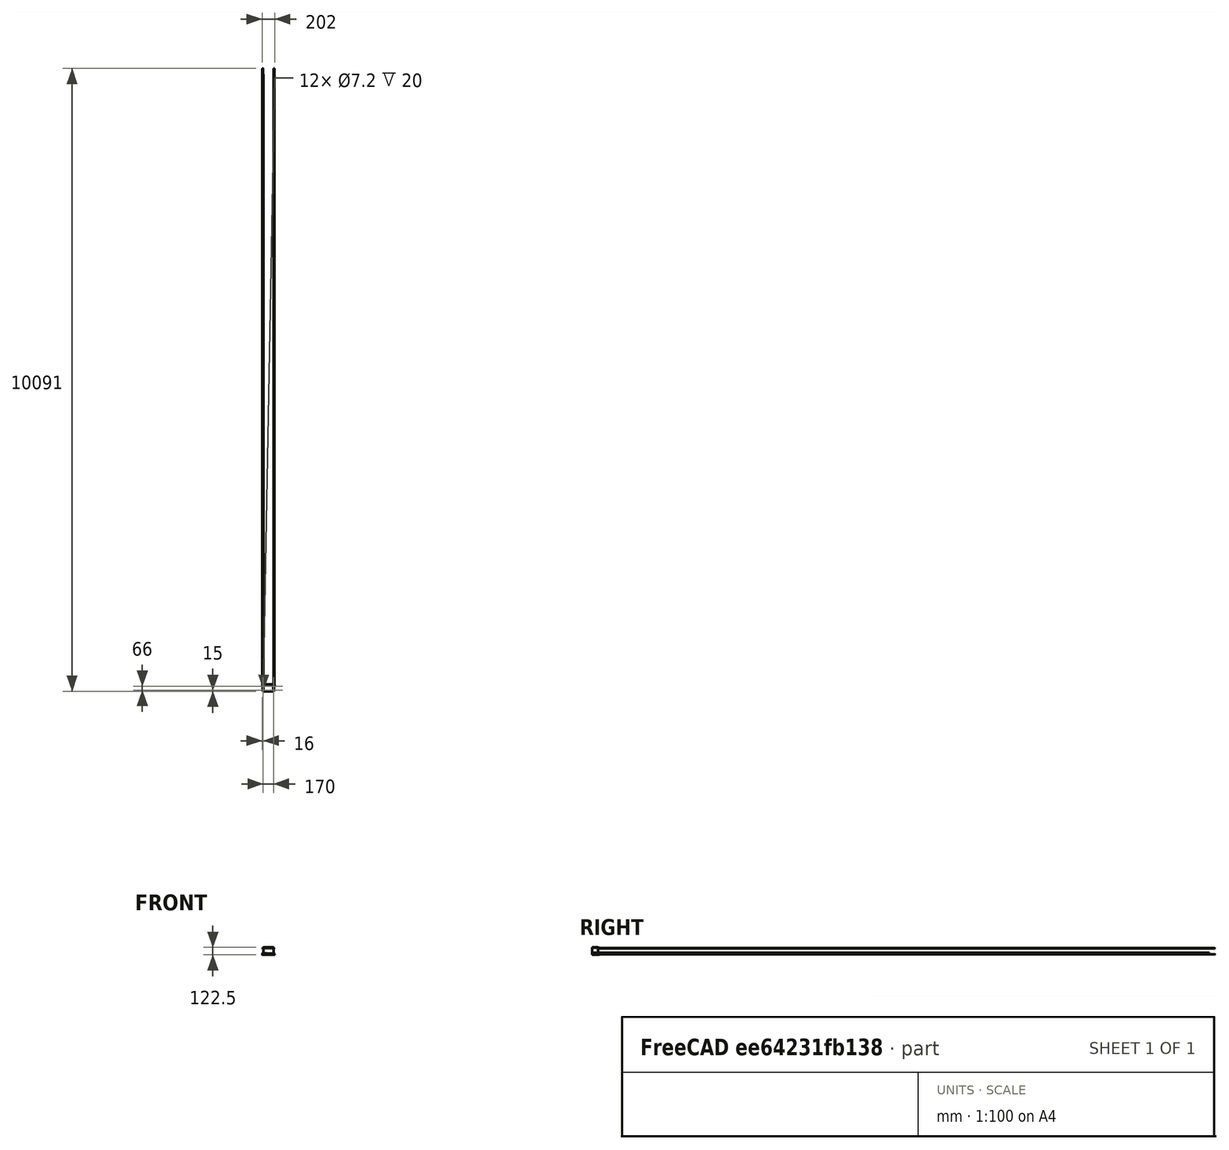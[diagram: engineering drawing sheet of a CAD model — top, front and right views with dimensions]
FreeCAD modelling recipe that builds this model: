
FCSTD DOCUMENT  (FreeCAD 0.15R4671 (Git))
Label: EBOX_Bottom
License: All rights reserved
LicenseURL: http://en.wikipedia.org/wiki/All_rights_reserved
objects: Sketcher::SketchObject×14, PartDesign::Pocket×9, PartDesign::Fillet×6, Mesh::Feature×5, PartDesign::Pad×5, Part::Feature×4
note: 52 computed .brp shape members not serialized (recipe doc carries the construction recipe); baked Part::Feature solids carry a one-line shape summary decoded from their .brp

FEATURE [Part::Feature] Part__Feature003  label="MKS_Gen_V1p3"
  Placement = pos=(4,-58,9) rot=(0,0,1;0rad)
  shape: bbox 143.1 x 84.2 x 22.31 mm, 8746 faces, 0 solids (baked)
FEATURE [Part::Feature] Part__Feature  label="OB1515_180mm"
  Placement = pos=(-90,0,0) rot=(0,1,0;1.5708rad)
  shape: bbox 180 x 15 x 15 mm, 158 faces (baked)
FEATURE [Part::Feature] Part__Feature004  label="OB1515_180mm001"
  Placement = pos=(-90,0,100) rot=(0,1,0;1.5708rad)
  shape: bbox 180 x 15 x 15 mm, 158 faces (baked)
FEATURE [Mesh::Feature] _0mmFan  label="40mmFan"
  Placement = pos=(15,-41,56) rot=(0,0,1;0rad)
FEATURE [Sketcher::SketchObject] Sketch
  Placement = pos=(0,0,-7.5) rot=(0,0,1;0rad)
  sketch-geometry (4):
    g0: LineSegment StartX=82 StartY=-8 StartZ=0 EndX=-82 EndY=-8 EndZ=0
    g1: LineSegment StartX=-82 StartY=-8 StartZ=0 EndX=-82 EndY=-106 EndZ=0
    g2: LineSegment StartX=-82 StartY=-106 StartZ=0 EndX=82 EndY=-106 EndZ=0
    g3: LineSegment StartX=82 StartY=-106 StartZ=0 EndX=82 EndY=-8 EndZ=0
  constraints (8):
    c: Coincident(g0,g1)
    c: Coincident(g1,g2)
    c: Coincident(g2,g3)
    c: Coincident(g3,g0)
    c: Horizontal(g0)
    c: Horizontal(g2)
    c: Vertical(g1)
    c: Vertical(g3)
FEATURE [PartDesign::Pad] Pad
  Length = 115
  Length2 = 100
  Placement = pos=(0,0,-7.5) rot=(0,0,1;0rad)
  Sketch = -> Sketch
  Type = 0
FEATURE [Sketcher::SketchObject] Sketch001
  Placement = pos=(0,0,107.5) rot=(0,0,1;0rad)
  Support = -> Pad [Face6]
  sketch-geometry (4):
    g0: LineSegment StartX=-79 StartY=-11 StartZ=0 EndX=79 EndY=-11 EndZ=0
    g1: LineSegment StartX=79 StartY=-11 StartZ=0 EndX=79 EndY=-103 EndZ=0
    g2: LineSegment StartX=79 StartY=-103 StartZ=0 EndX=-79 EndY=-103 EndZ=0
    g3: LineSegment StartX=-79 StartY=-103 StartZ=0 EndX=-79 EndY=-11 EndZ=0
  constraints (8):
    c: Coincident(g0,g1)
    c: Coincident(g1,g2)
    c: Coincident(g2,g3)
    c: Coincident(g3,g0)
    c: Horizontal(g0)
    c: Horizontal(g2)
    c: Vertical(g1)
    c: Vertical(g3)
FEATURE [PartDesign::Pocket] Pocket
  Length = 112
  Placement = pos=(0,0,-7.5) rot=(0,0,1;0rad)
  Sketch = -> Sketch001
  Type = 0
FEATURE [Sketcher::SketchObject] Sketch002
  Placement = pos=(0,0,-4.5) rot=(0,0,1;0rad)
  Support = -> Pocket [Face11]
  sketch-geometry (4):
    g0: Circle CenterX=71.2811 CenterY=-20.1362 CenterZ=0 NormalX=0 NormalY=0 NormalZ=1 Radius=4
    g1: Circle CenterX=71.2541 CenterY=-95.8403 CenterZ=0 NormalX=0 NormalY=0 NormalZ=1 Radius=4
    g2: Circle CenterX=-63.2692 CenterY=-95.845 CenterZ=0 NormalX=0 NormalY=0 NormalZ=1 Radius=4
    g3: Circle CenterX=-63.279 CenterY=-20.1649 CenterZ=0 NormalX=0 NormalY=0 NormalZ=1 Radius=4
  constraints (4):
    c: Radius(g0) = 4
    c: Equal(g0,g1)
    c: Equal(g0,g2)
    c: Equal(g0,g3)
FEATURE [PartDesign::Pad] Pad001
  Length = 13.5
  Length2 = 100
  Placement = pos=(0,0,-7.5) rot=(0,0,1;0rad)
  Sketch = -> Sketch002
  Type = 0
FEATURE [Sketcher::SketchObject] Sketch003
  Placement = pos=(0,0,9) rot=(0,0,1;0rad)
  Support = -> Pad001 [Face17]
  sketch-geometry (4):
    g0: Circle CenterX=-63.2989 CenterY=-20.1665 CenterZ=0 NormalX=0 NormalY=0 NormalZ=1 Radius=1.5
    g1: Circle CenterX=71.3054 CenterY=-20.1275 CenterZ=0 NormalX=0 NormalY=0 NormalZ=1 Radius=1.5
    g2: Circle CenterX=71.282 CenterY=-95.8363 CenterZ=0 NormalX=0 NormalY=0 NormalZ=1 Radius=1.5
    g3: Circle CenterX=-63.2831 CenterY=-95.8609 CenterZ=0 NormalX=0 NormalY=0 NormalZ=1 Radius=1.5
  constraints (4):
    c: Radius(g0) = 1.5
    c: Equal(g0,g1)
    c: Equal(g0,g2)
    c: Equal(g0,g3)
FEATURE [PartDesign::Pocket] Pocket001
  Length = 8
  Placement = pos=(0,0,-7.5) rot=(0,0,1;0rad)
  Sketch = -> Sketch003
  Type = 0
FEATURE [Sketcher::SketchObject] Sketch004
  Placement = pos=(0,0,107.5) rot=(0,0,1;0rad)
  Support = -> Pocket001 [Face5]
  sketch-geometry (4):
    g0: LineSegment StartX=-82 StartY=-106 StartZ=0 EndX=82 EndY=-106 EndZ=0
    g1: LineSegment StartX=82 StartY=-106 StartZ=0 EndX=82 EndY=-8 EndZ=0
    g2: LineSegment StartX=82 StartY=-8 StartZ=0 EndX=-82 EndY=-8 EndZ=0
    g3: LineSegment StartX=-82 StartY=-8 StartZ=0 EndX=-82 EndY=-106 EndZ=0
  constraints (8):
    c: Coincident(g0,g1)
    c: Coincident(g1,g2)
    c: Coincident(g2,g3)
    c: Coincident(g3,g0)
    c: Horizontal(g0)
    c: Horizontal(g2)
    c: Vertical(g1)
    c: Vertical(g3)
FEATURE [PartDesign::Pad] Pad002
  Length = 3
  Length2 = 100
  Placement = pos=(0,0,-7.5) rot=(0,0,1;0rad)
  Reversed = true
  Sketch = -> Sketch004
  Type = 0
FEATURE [Part::Feature] Pad002001  label="Pad003"
  shape: bbox 164 x 98 x 115 mm, 28 faces (baked)
FEATURE [Sketcher::SketchObject] Sketch005
  Placement = pos=(0,0,-7.5) rot=(1,0,0;3.14159rad)
  Support = -> Pad002001 [Face1]
  sketch-geometry (16):
    g0: ArcOfCircle CenterX=84 CenterY=25 CenterZ=0 NormalX=0 NormalY=0 NormalZ=1 Radius=7 StartAngle=4.71239 EndAngle=7.85398
    g1: ArcOfCircle CenterX=84 CenterY=91 CenterZ=0 NormalX=0 NormalY=0 NormalZ=1 Radius=7 StartAngle=4.71239 EndAngle=7.85398
    g2: ArcOfCircle CenterX=-84 CenterY=91 CenterZ=0 NormalX=0 NormalY=0 NormalZ=1 Radius=7 StartAngle=1.5708 EndAngle=4.71239
    g3: ArcOfCircle CenterX=-84 CenterY=25 CenterZ=0 NormalX=0 NormalY=0 NormalZ=1 Radius=7 StartAngle=1.5708 EndAngle=4.71239
    g4: LineSegment StartX=-84 StartY=32 StartZ=0 EndX=-81 EndY=32 EndZ=0
    g5: LineSegment StartX=-81 StartY=32 StartZ=0 EndX=-81 EndY=18 EndZ=0
    g6: LineSegment StartX=-81 StartY=18 StartZ=0 EndX=-84 EndY=18 EndZ=0
    g7: LineSegment StartX=-84 StartY=98 StartZ=0 EndX=-81 EndY=98 EndZ=0
    g8: LineSegment StartX=-81 StartY=98 StartZ=0 EndX=-81 EndY=84 EndZ=0
    g9: LineSegment StartX=-81 StartY=84 StartZ=0 EndX=-84 EndY=84 EndZ=0
    g10: LineSegment StartX=84 StartY=98 StartZ=0 EndX=81 EndY=98 EndZ=0
    g11: LineSegment StartX=81 StartY=98 StartZ=0 EndX=81 EndY=84 EndZ=0
    g12: LineSegment StartX=81 StartY=84 StartZ=0 EndX=84 EndY=84 EndZ=0
    g13: LineSegment StartX=84 StartY=32 StartZ=0 EndX=81 EndY=32 EndZ=0
    g14: LineSegment StartX=81 StartY=32 StartZ=0 EndX=81 EndY=18 EndZ=0
    g15: LineSegment StartX=81 StartY=18 StartZ=0 EndX=84 EndY=18 EndZ=0
  constraints (25):
    c: Tangent(g3,g4) = 1.5708
    c: Coincident(g4,g5)
    c: Vertical(g5)
    c: Coincident(g5,g6)
    c: Coincident(g6,g3)
    c: Horizontal(g6)
    c: Tangent(g6,g3)
    c: Tangent(g2,g7) = 1.5708
    c: Coincident(g7,g8)
    c: Vertical(g8)
    c: Coincident(g8,g9)
    c: Coincident(g9,g2)
    c: Horizontal(g9)
    c: Tangent(g1,g10) = -1.5708
    c: Coincident(g10,g11)
    c: Vertical(g11)
    c: Coincident(g11,g12)
    c: Coincident(g12,g1)
    c: Horizontal(g12)
    c: Tangent(g0,g13) = -1.5708
    c: Coincident(g13,g14)
    c: Vertical(g14)
    c: Coincident(g14,g15)
    c: Coincident(g15,g0)
    c: Horizontal(g15)
FEATURE [PartDesign::Pad] Pad002002
  Length = 35
  Length2 = 100
  Reversed = true
  Sketch = -> Sketch005
  Type = 0
FEATURE [PartDesign::Fillet] Fillet
  Base = -> Pad002002 [Edge28,Edge26,Edge22,Edge24,Edge8,Edge12,Edge14,Edge10]
  Radius = 1.99
FEATURE [Sketcher::SketchObject] Sketch006
  Placement = pos=(0,-106,0) rot=(1,0,0;1.5708rad)
  Support = -> Fillet [Face7]
  sketch-geometry (10):
    g0: LineSegment StartX=-82 StartY=29 StartZ=0 EndX=-82 EndY=27 EndZ=0
    g1: LineSegment StartX=-82 StartY=27 StartZ=0 EndX=-91 EndY=18 EndZ=0
    g2: LineSegment StartX=-91 StartY=18 StartZ=0 EndX=-92 EndY=18 EndZ=0
    g3: LineSegment StartX=-92 StartY=18 StartZ=0 EndX=-92 EndY=29 EndZ=0
    g4: LineSegment StartX=-92 StartY=29 StartZ=0 EndX=-82 EndY=29 EndZ=0
    g5: LineSegment StartX=82 StartY=29 StartZ=0 EndX=82 EndY=27 EndZ=0
    g6: LineSegment StartX=82 StartY=27 StartZ=0 EndX=91 EndY=18 EndZ=0
    g7: LineSegment StartX=91 StartY=18 StartZ=0 EndX=92 EndY=18 EndZ=0
    g8: LineSegment StartX=92 StartY=18 StartZ=0 EndX=92 EndY=29 EndZ=0
    g9: LineSegment StartX=92 StartY=29 StartZ=0 EndX=82 EndY=29 EndZ=0
  constraints (18):
    c: Vertical(g0)
    c: Coincident(g0,g1)
    c: Coincident(g1,g2)
    c: Horizontal(g2)
    c: Coincident(g2,g3)
    c: Vertical(g3)
    c: Coincident(g3,g4)
    c: Coincident(g4,g0)
    c: Horizontal(g4)
    c: Vertical(g5)
    c: Coincident(g5,g6)
    c: Coincident(g6,g7)
    c: Horizontal(g7)
    c: Coincident(g7,g8)
    c: Vertical(g8)
    c: Coincident(g8,g9)
    c: Coincident(g9,g5)
    c: Horizontal(g9)
FEATURE [PartDesign::Pocket] Pocket002
  Length = 5
  Sketch = -> Sketch006
  Type = 1
FEATURE [Mesh::Feature] HexNutStyle1_M3
  Placement = pos=(86.28,1.15,-100) rot=(0,0,1;0.523599rad)
FEATURE [Mesh::Feature] HexNutStyle1_M
  Placement = pos=(86.28,-64.85,-100) rot=(0,0,1;0.523599rad)
FEATURE [Mesh::Feature] HexNutStyle1_M004
  Placement = pos=(-83.72,1.15,-100) rot=(0,0,1;0.523599rad)
FEATURE [Mesh::Feature] HexNutStyle1_M005
  Placement = pos=(-83.72,-64.85,-100) rot=(0,0,1;0.523599rad)
FEATURE [Sketcher::SketchObject] Sketch007
  Placement = pos=(0,0,-7.5) rot=(1,0,0;3.14159rad)
  Support = -> Pocket002 [Face2]
  sketch-geometry (4):
    g0: Circle CenterX=-85 CenterY=91 CenterZ=0 NormalX=0 NormalY=0 NormalZ=1 Radius=1.8
    g1: Circle CenterX=-85 CenterY=25 CenterZ=0 NormalX=0 NormalY=0 NormalZ=1 Radius=1.8
    g2: Circle CenterX=85 CenterY=25 CenterZ=0 NormalX=0 NormalY=0 NormalZ=1 Radius=1.8
    g3: Circle CenterX=85 CenterY=91 CenterZ=0 NormalX=0 NormalY=0 NormalZ=1 Radius=1.8
  constraints (4):
    c: Radius(g0) = 1.8
    c: Equal(g0,g1)
    c: Equal(g0,g2)
    c: Equal(g0,g3)
FEATURE [PartDesign::Pocket] Pocket003
  Length = 28
  Sketch = -> Sketch007
  Type = 0
FEATURE [Sketcher::SketchObject] Sketch008
  Placement = pos=(0,0,-7.5) rot=(1,0,0;3.14159rad)
  Support = -> Pocket003 [Face2]
  sketch-geometry (4):
    g0: Circle CenterX=85 CenterY=91 CenterZ=0 NormalX=0 NormalY=0 NormalZ=1 Radius=3.6
    g1: Circle CenterX=85 CenterY=25 CenterZ=0 NormalX=0 NormalY=0 NormalZ=1 Radius=3.6
    g2: Circle CenterX=-85 CenterY=91 CenterZ=0 NormalX=0 NormalY=0 NormalZ=1 Radius=3.6
    g3: Circle CenterX=-85 CenterY=25 CenterZ=0 NormalX=0 NormalY=0 NormalZ=1 Radius=3.6
  constraints (4):
    c: Radius(g0) = 3.6
    c: Equal(g0,g1)
    c: Equal(g0,g2)
    c: Equal(g0,g3)
FEATURE [PartDesign::Pocket] Pocket004
  Length = 20
  Sketch = -> Sketch008
  Type = 0
FEATURE [Sketcher::SketchObject] Sketch009
  Placement = pos=(0,-8,0) rot=(0,0.707107,0.707107;3.14159rad)
  Support = -> Pocket004 [Face1]
  sketch-geometry (16):
    g0: LineSegment StartX=-81 StartY=7.5 StartZ=0 EndX=-101 EndY=7.5 EndZ=0
    g1: LineSegment StartX=-101 StartY=7.5 StartZ=0 EndX=-101 EndY=-7.5 EndZ=0
    g2: LineSegment StartX=-101 StartY=-7.5 StartZ=0 EndX=-81 EndY=-7.5 EndZ=0
    g3: LineSegment StartX=-81 StartY=-7.5 StartZ=0 EndX=-81 EndY=7.5 EndZ=0
    g4: LineSegment StartX=81 StartY=7.5 StartZ=0 EndX=101 EndY=7.5 EndZ=0
    g5: LineSegment StartX=101 StartY=7.5 StartZ=0 EndX=101 EndY=-7.5 EndZ=0
    g6: LineSegment StartX=101 StartY=-7.5 StartZ=0 EndX=81 EndY=-7.5 EndZ=0
    g7: LineSegment StartX=81 StartY=-7.5 StartZ=0 EndX=81 EndY=7.5 EndZ=0
    g8: LineSegment StartX=-92 StartY=107.5 StartZ=0 EndX=-81 EndY=107.5 EndZ=0
    g9: LineSegment StartX=-81 StartY=107.5 StartZ=0 EndX=-81 EndY=92.5 EndZ=0
    g10: LineSegment StartX=-81 StartY=92.5 StartZ=0 EndX=-92 EndY=92.5 EndZ=0
    g11: LineSegment StartX=-92 StartY=92.5 StartZ=0 EndX=-92 EndY=107.5 EndZ=0
    g12: LineSegment StartX=81 StartY=92.5 StartZ=0 EndX=92 EndY=92.5 EndZ=0
    g13: LineSegment StartX=92 StartY=92.5 StartZ=0 EndX=92 EndY=107.5 EndZ=0
    g14: LineSegment StartX=92 StartY=107.5 StartZ=0 EndX=81 EndY=107.5 EndZ=0
    g15: LineSegment StartX=81 StartY=107.5 StartZ=0 EndX=81 EndY=92.5 EndZ=0
  constraints (32):
    c: Coincident(g0,g1)
    c: Coincident(g1,g2)
    c: Coincident(g2,g3)
    c: Coincident(g3,g0)
    c: Horizontal(g0)
    c: Horizontal(g2)
    c: Vertical(g1)
    c: Vertical(g3)
    c: Coincident(g4,g5)
    c: Coincident(g5,g6)
    c: Coincident(g6,g7)
    c: Coincident(g7,g4)
    c: Horizontal(g4)
    c: Horizontal(g6)
    c: Vertical(g5)
    c: Vertical(g7)
    c: Coincident(g8,g9)
    c: Coincident(g9,g10)
    c: Coincident(g10,g11)
    c: Coincident(g11,g8)
    c: Horizontal(g8)
    c: Horizontal(g10)
    c: Vertical(g9)
    c: Vertical(g11)
    c: Coincident(g12,g13)
    c: Coincident(g13,g14)
    c: Coincident(g14,g15)
    c: Coincident(g15,g12)
    c: Horizontal(g12)
    c: Horizontal(g14)
    c: Vertical(g13)
    c: Vertical(g15)
FEATURE [PartDesign::Pad] Pad002003
  Length = 7
  Length2 = 100
  Reversed = true
  Sketch = -> Sketch009
  Type = 0
FEATURE [PartDesign::Fillet] Fillet001
  Base = -> Pad002003 [Edge22,Edge63]
  Radius = 4
FEATURE [PartDesign::Fillet] Fillet002
  Base = -> Fillet001 [Edge111,Edge77,Edge88,Edge51,Edge112,Edge78,Edge128,Edge92]
  Radius = 4
FEATURE [PartDesign::Fillet] Fillet003
  Base = -> Fillet002 [Edge120,Edge46]
  Radius = 4
FEATURE [Sketcher::SketchObject] Sketch010
  Placement = pos=(0,-15,0) rot=(1,0,0;1.5708rad)
  Support = -> Fillet003 [Face35]
  sketch-geometry (4):
    g0: Circle CenterX=-87.5 CenterY=100 CenterZ=0 NormalX=0 NormalY=0 NormalZ=1 Radius=1.8
    g1: Circle CenterX=87.5 CenterY=100 CenterZ=0 NormalX=0 NormalY=0 NormalZ=1 Radius=1.8
    g2: Circle CenterX=95 CenterY=0 CenterZ=0 NormalX=0 NormalY=0 NormalZ=1 Radius=1.8
    g3: Circle CenterX=-95 CenterY=0 CenterZ=0 NormalX=0 NormalY=0 NormalZ=1 Radius=1.8
  constraints (6):
    c: PointOnObject(g2,g-1)
    c: PointOnObject(g3,g-1)
    c: Radius(g0) = 1.8
    c: Equal(g0,g1)
    c: Equal(g0,g2)
    c: Equal(g0,g3)
FEATURE [PartDesign::Pocket] Pocket005
  Length = 5
  Sketch = -> Sketch010
  Type = 1
FEATURE [Sketcher::SketchObject] Sketch011
  Placement = pos=(0,-15,0) rot=(1,0,0;1.5708rad)
  Support = -> Pocket005 [Face31]
  sketch-geometry (4):
    g0: Circle CenterX=-87.5 CenterY=100 CenterZ=0 NormalX=0 NormalY=0 NormalZ=1 Radius=3.5
    g1: Circle CenterX=87.5 CenterY=100 CenterZ=0 NormalX=0 NormalY=0 NormalZ=1 Radius=3.5
    g2: Circle CenterX=95 CenterY=0 CenterZ=0 NormalX=0 NormalY=0 NormalZ=1 Radius=3.5
    g3: Circle CenterX=-95 CenterY=0 CenterZ=0 NormalX=0 NormalY=0 NormalZ=1 Radius=3.5
  constraints (6):
    c: PointOnObject(g2,g-1)
    c: PointOnObject(g3,g-1)
    c: Radius(g0) = 3.5
    c: Equal(g0,g1)
    c: Equal(g0,g2)
    c: Equal(g0,g3)
FEATURE [PartDesign::Pocket] Pocket006
  Length = 3
  Sketch = -> Sketch011
  Type = 0
FEATURE [PartDesign::Fillet] Fillet004
  Base = -> Pocket006 [Edge49,Edge45,Edge78,Edge79,Edge139]
  Radius = 1
FEATURE [Sketcher::SketchObject] Sketch012
  Placement = pos=(0,-106,0) rot=(1,0,0;1.5708rad)
  Support = -> Fillet004 [Face26]
  sketch-geometry (4):
    g0: LineSegment StartX=-46 StartY=21.5 StartZ=0 EndX=-33.5 EndY=21.5 EndZ=0
    g1: LineSegment StartX=-33.5 StartY=21.5 StartZ=0 EndX=-33.5 EndY=10.5 EndZ=0
    g2: LineSegment StartX=-33.5 StartY=10.5 StartZ=0 EndX=-46 EndY=10.5 EndZ=0
    g3: LineSegment StartX=-46 StartY=10.5 StartZ=0 EndX=-46 EndY=21.5 EndZ=0
  constraints (8):
    c: Coincident(g0,g1)
    c: Coincident(g1,g2)
    c: Coincident(g2,g3)
    c: Coincident(g3,g0)
    c: Horizontal(g0)
    c: Horizontal(g2)
    c: Vertical(g1)
    c: Vertical(g3)
FEATURE [PartDesign::Pocket] Pocket007
  Length = 5
  Sketch = -> Sketch012
  Type = 0
FEATURE [Sketcher::SketchObject] Sketch013
  Placement = pos=(0,-106,0) rot=(1,0,0;1.5708rad)
  Support = -> Pocket007 [Face22]
  sketch-geometry (4):
    g0: LineSegment StartX=-111 StartY=123 StartZ=0 EndX=97 EndY=123 EndZ=0
    g1: LineSegment StartX=97 StartY=123 StartZ=0 EndX=97 EndY=14.5 EndZ=0
    g2: LineSegment StartX=97 StartY=14.5 StartZ=0 EndX=-111 EndY=14.5 EndZ=0
    g3: LineSegment StartX=-111 StartY=14.5 StartZ=0 EndX=-111 EndY=123 EndZ=0
  constraints (8):
    c: Coincident(g0,g1)
    c: Coincident(g1,g2)
    c: Coincident(g2,g3)
    c: Coincident(g3,g0)
    c: Horizontal(g0)
    c: Horizontal(g2)
    c: Vertical(g1)
    c: Vertical(g3)
FEATURE [PartDesign::Pocket] Pocket008
  Length = 5
  Sketch = -> Sketch013
  Type = 1
FEATURE [PartDesign::Fillet] Fillet005  label="EBOX_Bottom"
  Base = -> Pocket008 [Edge180,Edge178,Edge176,Edge174]
  Radius = 3
